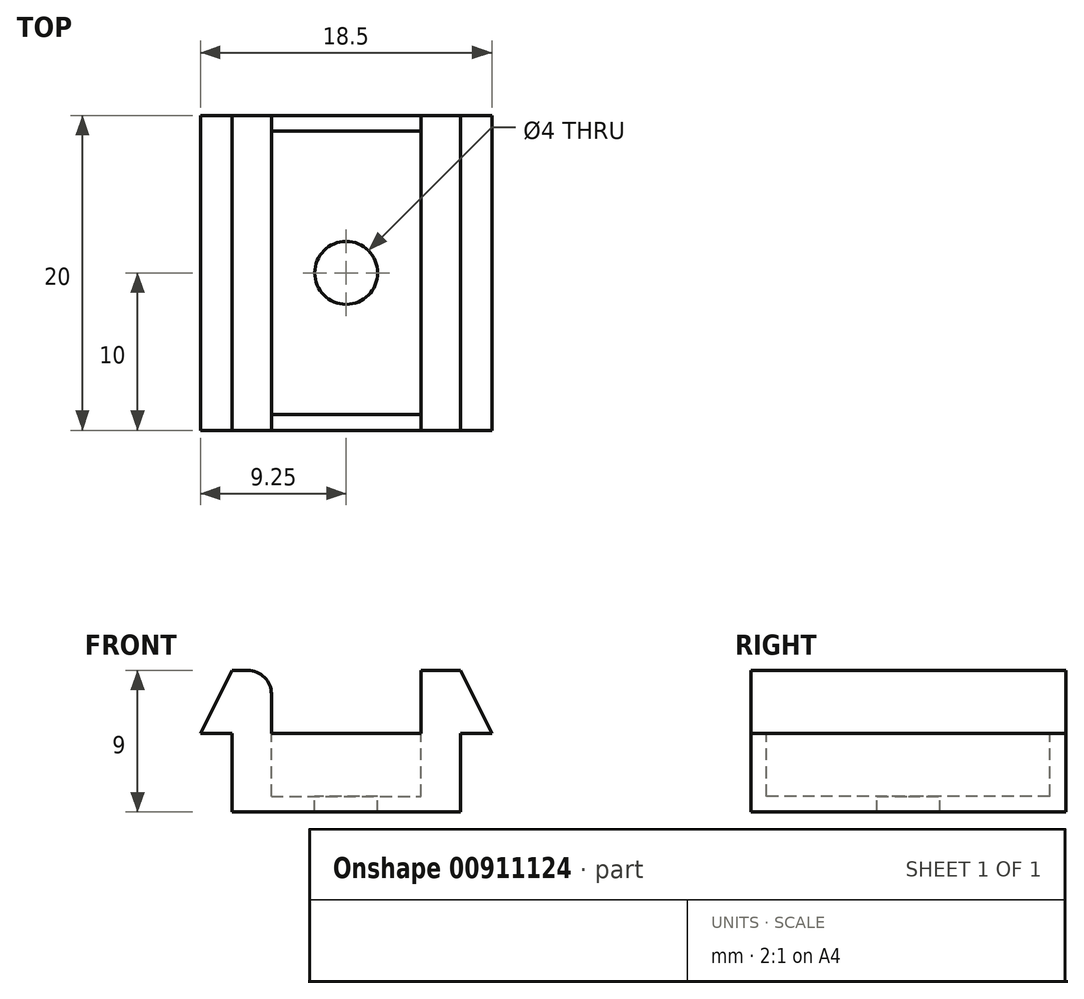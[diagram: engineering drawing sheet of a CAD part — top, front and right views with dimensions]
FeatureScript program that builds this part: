
annotation { "Feature Type Name" : "Feature", "Feature Type Description" : "" }
export const myFeature = defineFeature(function(context is Context, id is Id, definition is map)
    precondition{}
    {
        {
            var Q0;
            Q0=qCreatedBy(makeId("Top.planeOp"),FACE);
            var sketch = newSketch(context, id + "F0", { "sketchPlane" : qUnion([Q0])});
            skLineSegment(sketch, "E0.bottom", {"start": v(-9.25, 10) * mm, "end": v(9.25, 10) * mm});
            skLineSegment(sketch, "E0.top", {"start": v(-9.25, -10) * mm, "end": v(9.25, -10) * mm});
            skLineSegment(sketch, "E0.left", {"start": v(-9.25, 10) * mm, "end": v(-9.25, -10) * mm});
            skLineSegment(sketch, "E0.right", {"start": v(9.25, 10) * mm, "end": v(9.25, -10) * mm});
            skPoint(sketch, "E0.middle", {"position": v(0, 0) * mm});
            skSolve(sketch);
        }
        {
            var Q0;
            Q0=makeQuery(id+"F0.imprint","IMPRINT",FACE,{"disambiguationData":[TD([[makeQuery(id+"F0.imprint","IMPRINT",EDGE,{"derivedFrom":sQuery(id+"F0.wireOp",EDGE,"E0.bottom")}),-1.0]])]});
            extrude(context, id + "F1", {"entities" : qUnion([Q0]), "depth" : 9 * mm, "offsetDistance" : 25 * mm});
        }
        {
            var Q0;
            Q0=makeQuery(id+"F1.opExtrude","CAP_FACE",FACE,{"disambiguationData":[OSD([sQuery(id+"F0.wireOp",EDGE,"E0.bottom"),sQuery(id+"F0.wireOp",EDGE,"E0.top"),sQuery(id+"F0.wireOp",EDGE,"E0.left"),sQuery(id+"F0.wireOp",EDGE,"E0.right")])],"isStart":true});
            var sketch = newSketch(context, id + "F2", { "sketchPlane" : qUnion([Q0])});
            skLineSegment(sketch, "E1.0", {"start": v(7.25, -10) * mm, "end": v(7.25, 10) * mm});
            skLineSegment(sketch, "E2.0", {"start": v(-7.25, -10) * mm, "end": v(-7.25, 10) * mm});
            skSolve(sketch);
        }
        {
            var Q0;
            {var subQ0=sQuery(id+"F2.wireOp",EDGE,"E2.0");Q0=makeQuery(id+"F2.imprint","IMPRINT",FACE,{"disambiguationData":[TD([[makeQuery(id+"F2.imprint","IMPRINT",EDGE,{"derivedFrom":subQ0}),1.0]])]});}
            var Q1;
            {var subQ0=sQuery(id+"F2.wireOp",EDGE,"E1.0");Q1=makeQuery(id+"F2.imprint","IMPRINT",FACE,{"disambiguationData":[TD([[makeQuery(id+"F2.imprint","IMPRINT",EDGE,{"derivedFrom":subQ0}),-1.0]])]});}
            extrude(context, id + "F3", {"entities" : qUnion([Q0, Q1]), "operationType" : NewBodyOperationType.REMOVE, "oppositeDirection" : true, "depth" : 5 * mm, "offsetDistance" : 25 * mm});
        }
        {
            var Q0;
            Q0=makeQuery(id+"F1.opExtrude","CAP_FACE",FACE,{"disambiguationData":[OSD([sQuery(id+"F0.wireOp",EDGE,"E0.bottom"),sQuery(id+"F0.wireOp",EDGE,"E0.top"),sQuery(id+"F0.wireOp",EDGE,"E0.left"),sQuery(id+"F0.wireOp",EDGE,"E0.right")])],"isStart":false});
            var sketch = newSketch(context, id + "F4", { "sketchPlane" : qUnion([Q0])});
            skLineSegment(sketch, "E3.0", {"start": v(-9.5, 9) * mm, "end": v(9.5, 9) * mm});
            skLineSegment(sketch, "E4.0", {"start": v(-9.5, -9) * mm, "end": v(9.5, -9) * mm});
            skLineSegment(sketch, "E5.0", {"start": v(4.75, 10) * mm, "end": v(4.75, -10) * mm});
            skLineSegment(sketch, "E6.0", {"start": v(-4.75, 10) * mm, "end": v(-4.75, -10) * mm});
            skSolve(sketch);
        }
        {
            var Q0;
            {var subQ0=sQuery(id+"F4.wireOp",EDGE,"E6.0");var subQ1=sQuery(id+"F4.wireOp",EDGE,"E3.0");var subQ2=makeQuery(id+"F4.imprint","INTERSECT",VERTEX,{"derivedFrom":[subQ1,subQ0]});Q0=makeQuery(id+"F4.imprint","IMPRINT",FACE,{"disambiguationData":[TD([[makeQuery(id+"F4.imprint","IMPRINT",EDGE,{"disambiguationData":[TD([[subQ2,-1.0]])],"derivedFrom":subQ1}),-1.0]])]});}
            extrude(context, id + "F5", {"entities" : qUnion([Q0]), "operationType" : NewBodyOperationType.REMOVE, "oppositeDirection" : true, "depth" : 8 * mm, "offsetDistance" : 25 * mm});
        }
        {
            var Q0;
            Q0=makeQuery(id+"F1.opExtrude","CAP_FACE",FACE,{"disambiguationData":[OSD([sQuery(id+"F0.wireOp",EDGE,"E0.bottom"),sQuery(id+"F0.wireOp",EDGE,"E0.top"),sQuery(id+"F0.wireOp",EDGE,"E0.left"),sQuery(id+"F0.wireOp",EDGE,"E0.right")])],"isStart":false});
            var sketch = newSketch(context, id + "F6", { "sketchPlane" : qUnion([Q0])});
            skLineSegment(sketch, "E7", {"start": v(-4.75, -9) * mm, "end": v(-4.75, -10) * mm});
            skLineSegment(sketch, "E8", {"start": v(-4.75, -10) * mm, "end": v(4.75, -10) * mm});
            skLineSegment(sketch, "E9", {"start": v(4.75, -10) * mm, "end": v(4.75, -9) * mm});
            skLineSegment(sketch, "E10", {"start": v(4.75, -9) * mm, "end": v(-4.75, -9) * mm});
            skLineSegment(sketch, "E11", {"start": v(-4.75, 9) * mm, "end": v(-4.75, 10) * mm});
            skLineSegment(sketch, "E12", {"start": v(-4.75, 10) * mm, "end": v(4.75, 10) * mm});
            skLineSegment(sketch, "E13", {"start": v(4.75, 10) * mm, "end": v(4.75, 9) * mm});
            skLineSegment(sketch, "E14", {"start": v(4.75, 9) * mm, "end": v(-4.75, 9) * mm});
            skSolve(sketch);
        }
        {
            var Q0;
            Q0 = qSketchRegion(id + "F6", true);
            extrude(context, id + "F7", {"entities" : qUnion([Q0]), "operationType" : NewBodyOperationType.REMOVE, "oppositeDirection" : true, "depth" : 4 * mm, "offsetDistance" : 25 * mm});
        }
        {
            var Q0;
            Q0=makeQuery(id+"F5.boolean.opBoolean","COPY",FACE,{"derivedFrom":makeQuery(id+"F5.opExtrude","CAP_FACE",FACE,{"disambiguationData":[OSD([sQuery(id+"F4.wireOp",EDGE,"E3.0"),sQuery(id+"F4.wireOp",EDGE,"E4.0"),sQuery(id+"F4.wireOp",EDGE,"E5.0"),sQuery(id+"F4.wireOp",EDGE,"E6.0")])],"isStart":false})});
            var sketch = newSketch(context, id + "F8", { "sketchPlane" : qUnion([Q0])});
            skCircle(sketch, "E15", {"center": v(0, 0) * mm, "radius": 2 * mm});
            skSolve(sketch);
        }
        {
            var Q0;
            Q0 = qSketchRegion(id + "F8", true);
            extrude(context, id + "F9", {"entities" : qUnion([Q0]), "operationType" : NewBodyOperationType.REMOVE, "oppositeDirection" : true, "depth" : 25 * mm, "offsetDistance" : 25 * mm});
        }
        {
            var Q0;
            Q0=makeQuery(id+"F1.opExtrude","SWEPT_FACE",FACE,{"disambiguationData":[OSD([sQuery(id+"F0.wireOp",EDGE,"E0.top")])]});
            var sketch = newSketch(context, id + "F10", { "sketchPlane" : qUnion([Q0])});
            skLineSegment(sketch, "E16", {"start": v(0, 0) * mm, "end": v(0, 5) * mm, "construction": true});
            skLineSegment(sketch, "E17", {"start": v(-9.25, 5) * mm, "end": v(-7.25, 9) * mm});
            skLineSegment(sketch, "E18", {"start": v(9.25, 5) * mm, "end": v(7.25, 9) * mm});
            skSolve(sketch);
        }
        {
            var Q0;
            {var subQ0=sQuery(id+"F10.wireOp",EDGE,"E17");Q0=makeQuery(id+"F10.imprint","IMPRINT",FACE,{"disambiguationData":[TD([[makeQuery(id+"F10.imprint","IMPRINT",EDGE,{"derivedFrom":subQ0}),1.0]])]});}
            var Q1;
            {var subQ0=sQuery(id+"F10.wireOp",EDGE,"E18");Q1=makeQuery(id+"F10.imprint","IMPRINT",FACE,{"disambiguationData":[TD([[makeQuery(id+"F10.imprint","IMPRINT",EDGE,{"derivedFrom":subQ0}),-1.0]])]});}
            extrude(context, id + "F11", {"entities" : qUnion([Q0, Q1]), "operationType" : NewBodyOperationType.REMOVE, "endBound" : BoundingType.THROUGH_ALL, "oppositeDirection" : true, "depth" : 25 * mm, "offsetDistance" : 25 * mm});
        }
        {
            var Q0;
            Q0=makeQuery(id+"F7.boolean.opBoolean","MERGE",EDGE,{"derivedFrom":[makeQuery(id+"F5.boolean.opBoolean","COPY",EDGE,{"derivedFrom":makeQuery(id+"F5.opExtrude","CAP_EDGE",EDGE,{"disambiguationData":[OSD([sQuery(id+"F4.wireOp",EDGE,"E6.0")])],"isStart":true})})],"fromTools":[makeQuery(id+"F7.opExtrude","CAP_EDGE",EDGE,{"disambiguationData":[OSD([sQuery(id+"F6.wireOp",EDGE,"E7")])],"isStart":true}),makeQuery(id+"F7.opExtrude","CAP_EDGE",EDGE,{"disambiguationData":[OSD([sQuery(id+"F6.wireOp",EDGE,"E11")])],"isStart":true})]});
            var Q1;
            Q1=makeQuery(id+"F11.boolean.opBoolean","COPY",EDGE,{"derivedFrom":makeQuery(id+"F11.opExtrude","SWEPT_EDGE",EDGE,{"disambiguationData":[OSD([sQuery(id+"F0.wireOp",EDGE,"E0.top"),sQuery(id+"F10.wireOp",EDGE,"E17")])]})});
            var Q2;
            Q2=makeQuery(id+"F7.boolean.opBoolean","MERGE",EDGE,{"derivedFrom":[makeQuery(id+"F5.boolean.opBoolean","COPY",EDGE,{"derivedFrom":makeQuery(id+"F5.opExtrude","CAP_EDGE",EDGE,{"disambiguationData":[OSD([sQuery(id+"F4.wireOp",EDGE,"E5.0")])],"isStart":true})})],"fromTools":[makeQuery(id+"F7.opExtrude","CAP_EDGE",EDGE,{"disambiguationData":[OSD([sQuery(id+"F6.wireOp",EDGE,"E9")])],"isStart":true}),makeQuery(id+"F7.opExtrude","CAP_EDGE",EDGE,{"disambiguationData":[OSD([sQuery(id+"F6.wireOp",EDGE,"E13")])],"isStart":true})]});
            var Q3;
            Q3=makeQuery(id+"F11.boolean.opBoolean","COPY",EDGE,{"derivedFrom":makeQuery(id+"F11.opExtrude","SWEPT_EDGE",EDGE,{"disambiguationData":[OSD([sQuery(id+"F0.wireOp",EDGE,"E0.top"),sQuery(id+"F10.wireOp",EDGE,"E18")])]})});
            fillet(context, id + "F12", {"entities" : qUnion([Q0, Q1, Q2, Q3]), "radius" : 1.5 * mm, "tangentPropagation" : true, "allowEdgeOverflow" : false});
        }
    });
